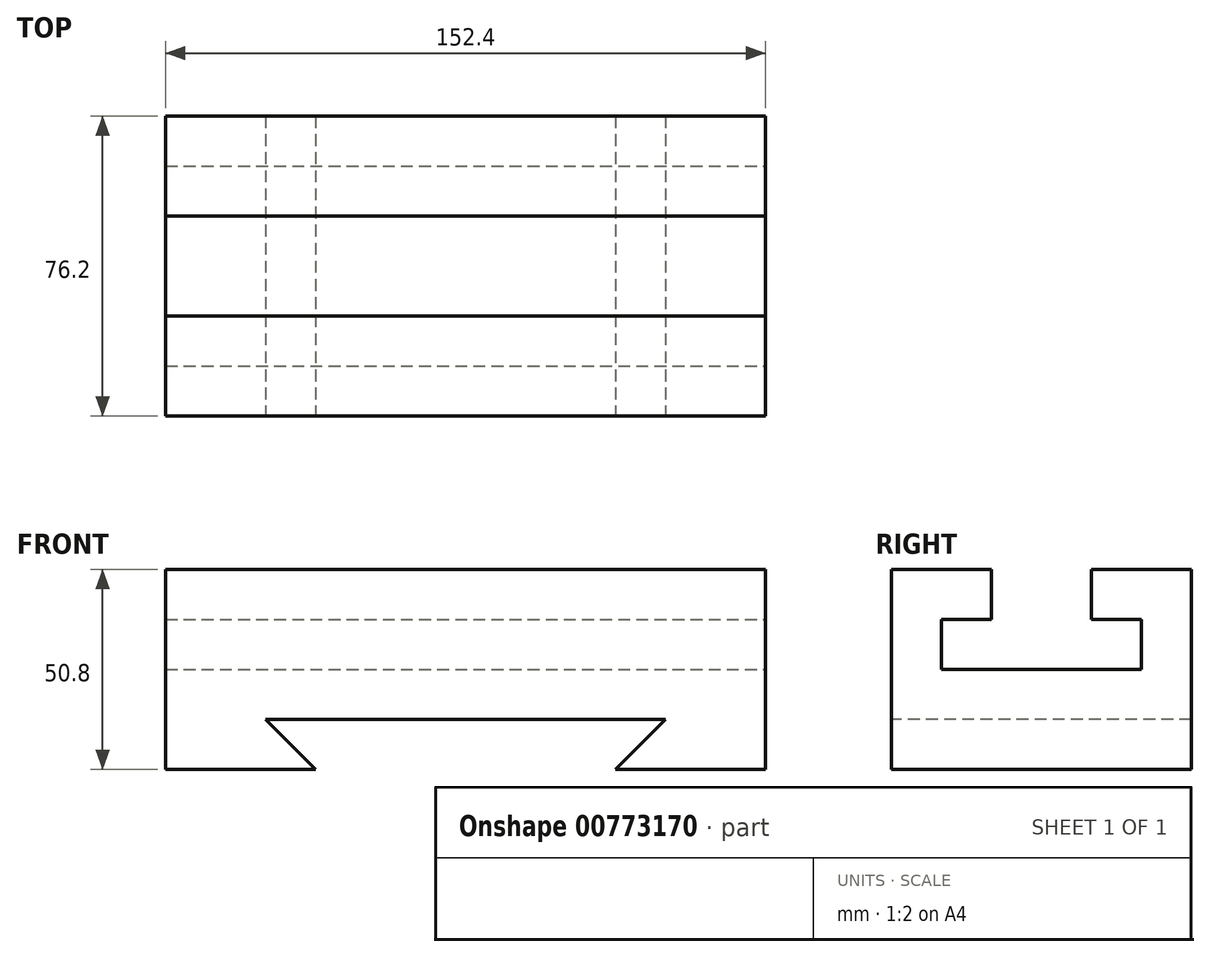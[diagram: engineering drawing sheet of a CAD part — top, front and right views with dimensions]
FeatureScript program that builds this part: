
annotation { "Feature Type Name" : "Feature", "Feature Type Description" : "" }
export const myFeature = defineFeature(function(context is Context, id is Id, definition is map)
    precondition{}
    {
        {
            var Q0;
            Q0=qCreatedBy(makeId("Front.planeOp"),FACE);
            var sketch = newSketch(context, id + "F0", { "sketchPlane" : qUnion([Q0])});
            skLineSegment(sketch, "E0", {"start": v(0, 0) * mm, "end": v(152.4, 0) * mm});
            skLineSegment(sketch, "E1", {"start": v(152.4, 0) * mm, "end": v(152.4, 50.8) * mm});
            skLineSegment(sketch, "E2", {"start": v(152.4, 50.8) * mm, "end": v(0, 50.8) * mm});
            skLineSegment(sketch, "E3", {"start": v(0, 50.8) * mm, "end": v(0, 0) * mm});
            skSolve(sketch);
        }
        {
            var Q0;
            Q0=makeQuery(id+"F0.imprint","IMPRINT",FACE,{"disambiguationData":[TD([[makeQuery(id+"F0.imprint","IMPRINT",EDGE,{"derivedFrom":sQuery(id+"F0.wireOp",EDGE,"E0")}),1.0]])]});
            extrude(context, id + "F1", {"entities" : qUnion([Q0]), "depth" : 76.2 * mm, "offsetDistance" : 25.4 * mm});
        }
        {
            var Q0;
            Q0=makeQuery(id+"F1.opExtrude","SWEPT_FACE",FACE,{"disambiguationData":[OSD([sQuery(id+"F0.wireOp",EDGE,"E1")])]});
            var sketch = newSketch(context, id + "F2", { "sketchPlane" : qUnion([Q0])});
            skLineSegment(sketch, "E4", {"start": v(-76.2, 50.8) * mm, "end": v(-50.8, 50.8) * mm});
            skLineSegment(sketch, "E5", {"start": v(-50.8, 50.8) * mm, "end": v(-50.8, 38.1) * mm});
            skLineSegment(sketch, "E6", {"start": v(-50.8, 38.1) * mm, "end": v(-63.5, 38.1) * mm});
            skLineSegment(sketch, "E7", {"start": v(-63.5, 38.1) * mm, "end": v(-63.5, 25.4) * mm});
            skLineSegment(sketch, "E8", {"start": v(-63.5, 25.4) * mm, "end": v(-12.7, 25.4) * mm});
            skLineSegment(sketch, "E9", {"start": v(-12.7, 25.4) * mm, "end": v(-12.7, 38.1) * mm});
            skLineSegment(sketch, "E10", {"start": v(-12.7, 38.1) * mm, "end": v(-25.4, 38.1) * mm});
            skLineSegment(sketch, "E11", {"start": v(-25.4, 38.1) * mm, "end": v(-25.4, 50.8) * mm});
            skSolve(sketch);
        }
        {
            var Q0;
            {var subQ0=sQuery(id+"F2.wireOp",EDGE,"E5");Q0=makeQuery(id+"F2.imprint","IMPRINT",FACE,{"disambiguationData":[TD([[makeQuery(id+"F2.imprint","IMPRINT",EDGE,{"derivedFrom":subQ0}),1.0]])]});}
            extrude(context, id + "F3", {"entities" : qUnion([Q0]), "operationType" : NewBodyOperationType.REMOVE, "oppositeDirection" : true, "depth" : 152.4 * mm, "offsetDistance" : 25.4 * mm});
        }
        {
            var Q0;
            Q0=makeQuery(id+"F1.opExtrude","CAP_FACE",FACE,{"disambiguationData":[OSD([sQuery(id+"F0.wireOp",EDGE,"E0"),sQuery(id+"F0.wireOp",EDGE,"E1"),sQuery(id+"F0.wireOp",EDGE,"E2"),sQuery(id+"F0.wireOp",EDGE,"E3")])],"isStart":false});
            var sketch = newSketch(context, id + "F4", { "sketchPlane" : qUnion([Q0])});
            skLineSegment(sketch, "E12", {"start": v(0, 0) * mm, "end": v(38.1, 0) * mm});
            skLineSegment(sketch, "E13", {"start": v(0, 0) * mm, "end": v(0, 12.7) * mm});
            skLineSegment(sketch, "E14", {"start": v(0, 12.7) * mm, "end": v(25.4, 12.7) * mm});
            skLineSegment(sketch, "E15", {"start": v(25.4, 12.7) * mm, "end": v(38.1, 0) * mm});
            skLineSegment(sketch, "E16", {"start": v(152.4, 0) * mm, "end": v(114.3, 0) * mm});
            skLineSegment(sketch, "E17", {"start": v(152.4, 0) * mm, "end": v(152.4, 12.7) * mm});
            skLineSegment(sketch, "E18", {"start": v(152.4, 12.7) * mm, "end": v(127, 12.7) * mm});
            skLineSegment(sketch, "E19", {"start": v(127, 12.7) * mm, "end": v(114.3, 0) * mm});
            skLineSegment(sketch, "E20", {"start": v(127, 12.7) * mm, "end": v(25.4, 12.7) * mm});
            skSolve(sketch);
        }
        {
            var Q0;
            {var subQ0=sQuery(id+"F4.wireOp",EDGE,"E15");Q0=makeQuery(id+"F4.imprint","IMPRINT",FACE,{"disambiguationData":[TD([[makeQuery(id+"F4.imprint","IMPRINT",EDGE,{"derivedFrom":subQ0}),1.0]])]});}
            extrude(context, id + "F5", {"entities" : qUnion([Q0]), "operationType" : NewBodyOperationType.REMOVE, "oppositeDirection" : true, "depth" : 76.2 * mm, "offsetDistance" : 25.4 * mm});
        }
    });
